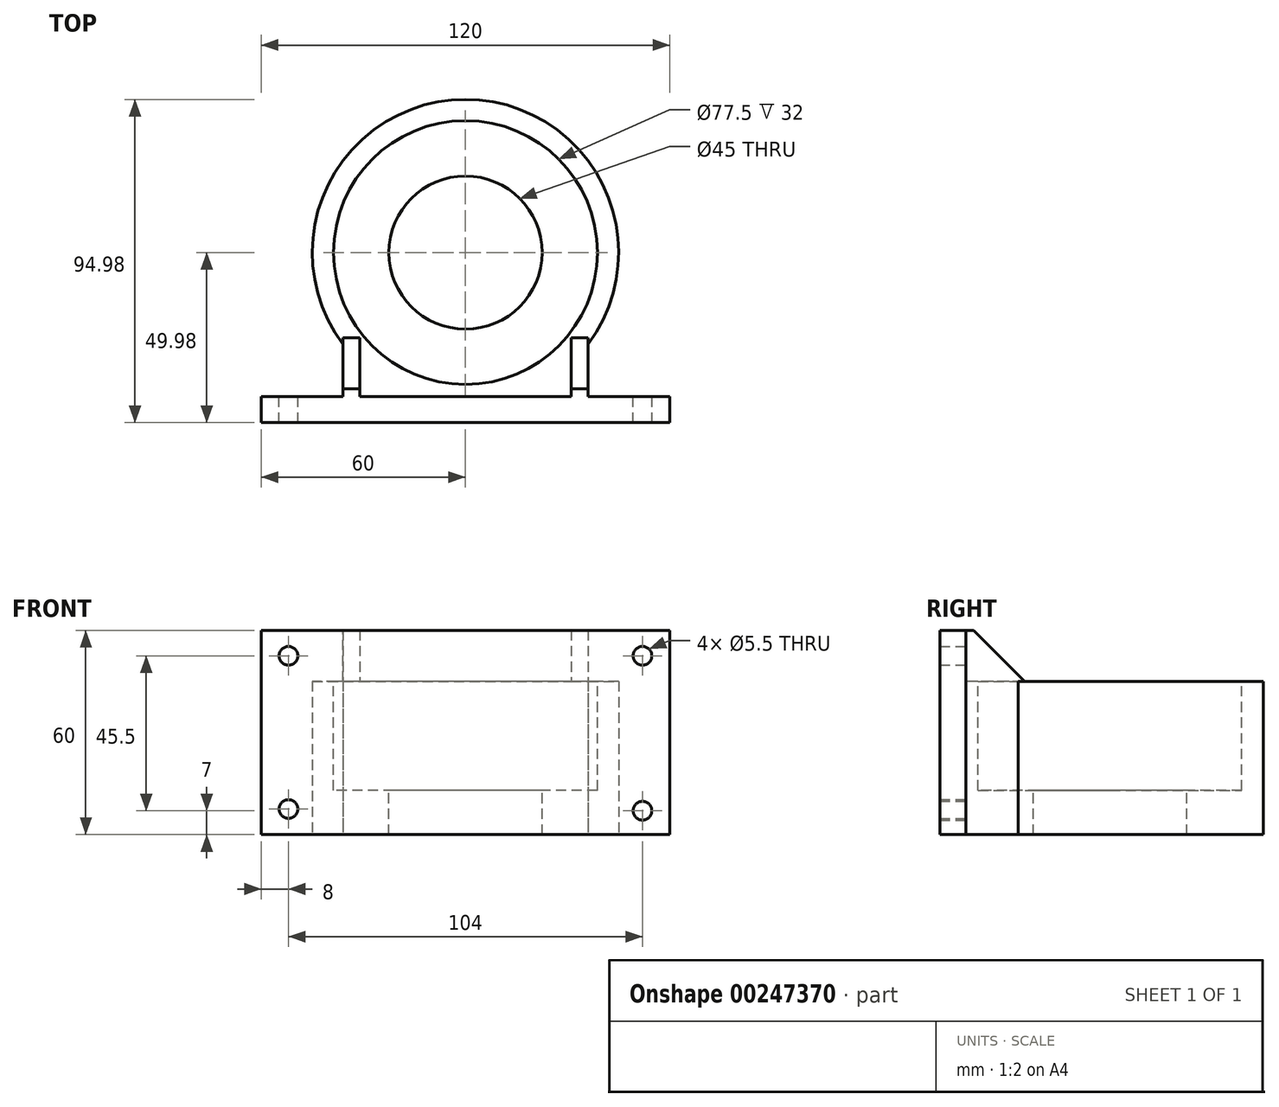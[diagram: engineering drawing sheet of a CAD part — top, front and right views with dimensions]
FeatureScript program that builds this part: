
annotation { "Feature Type Name" : "Feature", "Feature Type Description" : "" }
export const myFeature = defineFeature(function(context is Context, id is Id, definition is map)
    precondition{}
    {
        {
            var Q0;
            Q0=qCreatedBy(makeId("Top.planeOp"),FACE);
            var sketch = newSketch(context, id + "F0", { "sketchPlane" : qUnion([Q0])});
            skCircle(sketch, "E0", {"center": v(0, 0) * mm, "radius": 45 * mm});
            skLineSegment(sketch, "E1.bottom", {"start": v(-36, -27) * mm, "end": v(36, -27) * mm});
            skLineSegment(sketch, "E1.top", {"start": v(-36, -50) * mm, "end": v(36, -50) * mm});
            skLineSegment(sketch, "E1.left", {"start": v(-36, -27) * mm, "end": v(-36, -50) * mm});
            skLineSegment(sketch, "E1.right", {"start": v(36, -27) * mm, "end": v(36, -50) * mm});
            skLineSegment(sketch, "E2.bottom", {"start": v(-60, -42.37) * mm, "end": v(60, -42.37) * mm});
            skLineSegment(sketch, "E2.top", {"start": v(-60, -49.98) * mm, "end": v(60, -49.98) * mm});
            skLineSegment(sketch, "E2.left", {"start": v(-60, -42.37) * mm, "end": v(-60, -49.98) * mm});
            skLineSegment(sketch, "E2.right", {"start": v(60, -42.37) * mm, "end": v(60, -49.98) * mm});
            skSolve(sketch);
        }
        {
            var Q0;
            {var subQ0=sQuery(id+"F0.wireOp",EDGE,"E1.bottom");Q0=makeQuery(id+"F0.imprint","IMPRINT",FACE,{"disambiguationData":[TD([[makeQuery(id+"F0.imprint","IMPRINT",EDGE,{"derivedFrom":subQ0}),1.0]])]});}
            var Q1;
            {var subQ0=sQuery(id+"F0.wireOp",EDGE,"E1.left");var subQ3=sQuery(id+"F0.wireOp",EDGE,"E2.bottom");var subQ5=makeQuery(id+"F0.imprint","INTERSECT",VERTEX,{"derivedFrom":[subQ0,subQ3]});Q1=makeQuery(id+"F0.imprint","IMPRINT",FACE,{"disambiguationData":[TD([[makeQuery(id+"F0.imprint","IMPRINT",EDGE,{"disambiguationData":[TD([[subQ5,-1.0]])],"derivedFrom":subQ3}),1.0]])]});}
            var Q2;
            {var subQ0=sQuery(id+"F0.wireOp",EDGE,"E1.bottom");Q2=makeQuery(id+"F0.imprint","IMPRINT",FACE,{"disambiguationData":[TD([[makeQuery(id+"F0.imprint","IMPRINT",EDGE,{"derivedFrom":subQ0}),-1.0]])]});}
            var Q3;
            {var subQ0=sQuery(id+"F0.wireOp",EDGE,"E2.bottom");var subQ1=sQuery(id+"F0.wireOp",EDGE,"E0");var subQ2=makeQuery(id+"F0.imprint","INTERSECT",VERTEX,{"disambiguationData":[OD(0.0)],"derivedFrom":[subQ1,subQ0]});Q3=makeQuery(id+"F0.imprint","IMPRINT",FACE,{"disambiguationData":[TD([[makeQuery(id+"F0.imprint","IMPRINT",EDGE,{"disambiguationData":[TD([[subQ2,-1.0]])],"derivedFrom":subQ1}),1.0]])]});}
            var Q4;
            {var subQ5=sQuery(id+"F0.wireOp",EDGE,"E2.left");Q4=makeQuery(id+"F0.imprint","IMPRINT",FACE,{"disambiguationData":[TD([[makeQuery(id+"F0.imprint","IMPRINT",EDGE,{"derivedFrom":subQ5}),1.0]])]});}
            var Q5;
            {var subQ0=sQuery(id+"F0.wireOp",EDGE,"E2.bottom");var subQ3=sQuery(id+"F0.wireOp",EDGE,"E0");var subQ4=makeQuery(id+"F0.imprint","INTERSECT",VERTEX,{"disambiguationData":[OD(0.0)],"derivedFrom":[subQ3,subQ0]});Q5=makeQuery(id+"F0.imprint","IMPRINT",FACE,{"disambiguationData":[TD([[makeQuery(id+"F0.imprint","IMPRINT",EDGE,{"disambiguationData":[TD([[subQ4,-1.0]])],"derivedFrom":subQ3}),-1.0]])]});}
            var Q6;
            {var subQ5=sQuery(id+"F0.wireOp",EDGE,"E2.right");Q6=makeQuery(id+"F0.imprint","IMPRINT",FACE,{"disambiguationData":[TD([[makeQuery(id+"F0.imprint","IMPRINT",EDGE,{"derivedFrom":subQ5}),-1.0]])]});}
            var Q7;
            {var subQ0=sQuery(id+"F0.wireOp",EDGE,"E1.right");var subQ3=sQuery(id+"F0.wireOp",EDGE,"E2.bottom");var subQ5=makeQuery(id+"F0.imprint","INTERSECT",VERTEX,{"derivedFrom":[subQ0,subQ3]});Q7=makeQuery(id+"F0.imprint","IMPRINT",FACE,{"disambiguationData":[TD([[makeQuery(id+"F0.imprint","IMPRINT",EDGE,{"disambiguationData":[TD([[subQ5,1.0]])],"derivedFrom":subQ3}),1.0]])]});}
            extrude(context, id + "F1", {"entities" : qUnion([Q0, Q1, Q2, Q3, Q4, Q5, Q6, Q7]), "depth" : 45 * mm});
        }
        {
            var Q0;
            Q0=makeQuery(id+"F1.opExtrude","CAP_FACE",FACE,{"disambiguationData":[OSD([sQuery(id+"F0.wireOp",EDGE,"E0"),sQuery(id+"F0.wireOp",EDGE,"E1.left"),sQuery(id+"F0.wireOp",EDGE,"E1.right"),sQuery(id+"F0.wireOp",EDGE,"E2.bottom"),sQuery(id+"F0.wireOp",EDGE,"E2.top"),sQuery(id+"F0.wireOp",EDGE,"E2.left"),sQuery(id+"F0.wireOp",EDGE,"E2.right")])],"isStart":false});
            var sketch = newSketch(context, id + "F2", { "sketchPlane" : qUnion([Q0])});
            skCircle(sketch, "E3", {"center": v(0, 0) * mm, "radius": 38.75 * mm});
            skSolve(sketch);
        }
        {
            var Q0;
            Q0=makeQuery(id+"F1.opExtrude","CAP_FACE",FACE,{"disambiguationData":[OSD([sQuery(id+"F0.wireOp",EDGE,"E0"),sQuery(id+"F0.wireOp",EDGE,"E1.left"),sQuery(id+"F0.wireOp",EDGE,"E1.right"),sQuery(id+"F0.wireOp",EDGE,"E2.bottom"),sQuery(id+"F0.wireOp",EDGE,"E2.top"),sQuery(id+"F0.wireOp",EDGE,"E2.left"),sQuery(id+"F0.wireOp",EDGE,"E2.right")])],"isStart":false});
            var sketch = newSketch(context, id + "F3", { "sketchPlane" : qUnion([Q0])});
            skLineSegment(sketch, "E4.bottom", {"start": v(-60, -42.37) * mm, "end": v(60, -42.37) * mm});
            skLineSegment(sketch, "E4.top", {"start": v(-60, -49.98) * mm, "end": v(60, -49.98) * mm});
            skLineSegment(sketch, "E4.left", {"start": v(-60, -42.37) * mm, "end": v(-60, -49.98) * mm});
            skLineSegment(sketch, "E4.right", {"start": v(60, -42.37) * mm, "end": v(60, -49.98) * mm});
            skSolve(sketch);
        }
        {
            var Q0;
            Q0=qSketchRegion(id+"F2",true);
            extrude(context, id + "F4", {"entities" : qUnion([Q0]), "operationType" : NewBodyOperationType.REMOVE, "oppositeDirection" : true, "depth" : 32 * mm});
        }
        {
            var Q0;
            Q0=makeQuery(id+"F3.imprint","IMPRINT",FACE,{"disambiguationData":[TD([[makeQuery(id+"F3.imprint","IMPRINT",EDGE,{"derivedFrom":sQuery(id+"F3.wireOp",EDGE,"E4.top")}),1.0]])]});
            extrude(context, id + "F5", {"entities" : qUnion([Q0]), "operationType" : NewBodyOperationType.ADD, "depth" : 15 * mm});
        }
        {
            var Q0;
            Q0=makeQuery(id+"F1.opExtrude","CAP_FACE",FACE,{"disambiguationData":[OSD([sQuery(id+"F0.wireOp",EDGE,"E0"),sQuery(id+"F0.wireOp",EDGE,"E1.left"),sQuery(id+"F0.wireOp",EDGE,"E1.right"),sQuery(id+"F0.wireOp",EDGE,"E2.bottom"),sQuery(id+"F0.wireOp",EDGE,"E2.top"),sQuery(id+"F0.wireOp",EDGE,"E2.left"),sQuery(id+"F0.wireOp",EDGE,"E2.right")])],"isStart":false});
            var sketch = newSketch(context, id + "F6", { "sketchPlane" : qUnion([Q0])});
            skLineSegment(sketch, "E5.bottom", {"start": v(-36, -25.03) * mm, "end": v(-31, -25.03) * mm});
            skLineSegment(sketch, "E5.top", {"start": v(-36, -42.53) * mm, "end": v(-31, -42.53) * mm});
            skLineSegment(sketch, "E5.left", {"start": v(-36, -25.03) * mm, "end": v(-36, -42.53) * mm});
            skLineSegment(sketch, "E5.right", {"start": v(-31, -25.03) * mm, "end": v(-31, -42.53) * mm});
            skLineSegment(sketch, "E6.bottom", {"start": v(31, -25.03) * mm, "end": v(36, -25.03) * mm});
            skLineSegment(sketch, "E6.top", {"start": v(31, -42.53) * mm, "end": v(36, -42.53) * mm});
            skLineSegment(sketch, "E6.left", {"start": v(31, -25.03) * mm, "end": v(31, -42.53) * mm});
            skLineSegment(sketch, "E6.right", {"start": v(36, -25.03) * mm, "end": v(36, -42.53) * mm});
            skSolve(sketch);
        }
        {
            var Q0;
            {var subQ0=sQuery(id+"F6.wireOp",EDGE,"E5.bottom");Q0=makeQuery(id+"F6.imprint","IMPRINT",FACE,{"disambiguationData":[TD([[makeQuery(id+"F6.imprint","IMPRINT",EDGE,{"derivedFrom":subQ0}),-1.0]])]});}
            var Q1;
            {var subQ0=sQuery(id+"F6.wireOp",EDGE,"E6.bottom");Q1=makeQuery(id+"F6.imprint","IMPRINT",FACE,{"disambiguationData":[TD([[makeQuery(id+"F6.imprint","IMPRINT",EDGE,{"derivedFrom":subQ0}),-1.0]])]});}
            extrude(context, id + "F7", {"entities" : qUnion([Q0, Q1]), "operationType" : NewBodyOperationType.ADD, "depth" : 15 * mm});
        }
        {
            var Q0;
            Q0=makeQuery(id+"F7.opExtrude","CAP_EDGE",EDGE,{"disambiguationData":[OSD([sQuery(id+"F6.wireOp",EDGE,"E5.bottom")])],"isStart":false});
            var Q1;
            Q1=makeQuery(id+"F7.opExtrude","CAP_EDGE",EDGE,{"disambiguationData":[OSD([sQuery(id+"F6.wireOp",EDGE,"E6.bottom")])],"isStart":false});
            chamfer(context, id + "F8", {"entities" : qUnion([Q0, Q1]), "width" : 15 * mm, "tangentPropagation" : true});
        }
        {
            var Q0;
            {var subQ0=sQuery(id+"F0.wireOp",EDGE,"E2.left");var subQ1=sQuery(id+"F0.wireOp",EDGE,"E2.right");var subQ3=sQuery(id+"F0.wireOp",EDGE,"E2.bottom");var subQ5=sQuery(id+"F0.wireOp",EDGE,"E1.left");var subQ9=sQuery(id+"F3.wireOp",EDGE,"E4.bottom");Q0=makeQuery(id+"F7.boolean.opBoolean","SPLIT",FACE,{"disambiguationData":[TD([makeQuery(id+"F1.opExtrude","SWEPT_FACE",FACE,{"disambiguationData":[OSD([subQ5])]})])],"derivedFrom":makeQuery(id+"F5.boolean.opBoolean","MERGE",FACE,{"derivedFrom":[makeQuery(id+"F1.opExtrude","SWEPT_FACE",FACE,{"disambiguationData":[OSD([subQ3]),TDD([makeQuery(id+"F0.imprint","IMPRINT",EDGE,{"disambiguationData":[TD([[makeQuery(id+"F0.imprint","INTERSECT",VERTEX,{"derivedFrom":[subQ3,subQ0]}),-1.0]])],"derivedFrom":subQ3})])]}),makeQuery(id+"F1.opExtrude","SWEPT_FACE",FACE,{"disambiguationData":[OSD([subQ3]),TDD([makeQuery(id+"F0.imprint","IMPRINT",EDGE,{"disambiguationData":[TD([[makeQuery(id+"F0.imprint","INTERSECT",VERTEX,{"derivedFrom":[subQ3,subQ1]}),1.0]])],"derivedFrom":subQ3})])]}),makeQuery(id+"F5.opExtrude","SWEPT_FACE",FACE,{"disambiguationData":[OSD([subQ9])]})]})});}
            var sketch = newSketch(context, id + "F9", { "sketchPlane" : qUnion([Q0])});
            skCircle(sketch, "E7", {"center": v(52, 7.5) * mm, "radius": 2.75 * mm});
            skCircle(sketch, "E8", {"center": v(52, 52.5) * mm, "radius": 2.75 * mm});
            skCircle(sketch, "E9", {"center": v(-52, 7) * mm, "radius": 2.75 * mm});
            skCircle(sketch, "E10", {"center": v(-52, 52.5) * mm, "radius": 2.75 * mm});
            skSolve(sketch);
        }
        {
            var Q0;
            Q0=makeQuery(id+"F9.imprint","IMPRINT",FACE,{"disambiguationData":[TD([[makeQuery(id+"F9.imprint","IMPRINT",EDGE,{"derivedFrom":sQuery(id+"F9.wireOp",EDGE,"E7")}),1.0]])]});
            var Q1;
            Q1=makeQuery(id+"F9.imprint","IMPRINT",FACE,{"disambiguationData":[TD([[makeQuery(id+"F9.imprint","IMPRINT",EDGE,{"derivedFrom":sQuery(id+"F9.wireOp",EDGE,"E8")}),1.0]])]});
            var Q2;
            Q2=makeQuery(id+"F9.imprint","IMPRINT",FACE,{"disambiguationData":[TD([[makeQuery(id+"F9.imprint","IMPRINT",EDGE,{"derivedFrom":sQuery(id+"F9.wireOp",EDGE,"E9")}),1.0]])]});
            var Q3;
            Q3=makeQuery(id+"F9.imprint","IMPRINT",FACE,{"disambiguationData":[TD([[makeQuery(id+"F9.imprint","IMPRINT",EDGE,{"derivedFrom":sQuery(id+"F9.wireOp",EDGE,"E10")}),1.0]])]});
            extrude(context, id + "F10", {"entities" : qUnion([Q0, Q1, Q2, Q3]), "operationType" : NewBodyOperationType.REMOVE, "oppositeDirection" : true, "depth" : 25 * mm});
        }
        {
            var Q0;
            Q0=makeQuery(id+"F4.boolean.opBoolean","COPY",FACE,{"derivedFrom":makeQuery(id+"F4.opExtrude","CAP_FACE",FACE,{"disambiguationData":[OSD([sQuery(id+"F2.wireOp",EDGE,"E3")])],"isStart":false})});
            var sketch = newSketch(context, id + "F11", { "sketchPlane" : qUnion([Q0])});
            skCircle(sketch, "E11", {"center": v(0, 0) * mm, "radius": 22.5 * mm});
            skSolve(sketch);
        }
        {
            var Q0;
            Q0=makeQuery(id+"F11.imprint","IMPRINT",FACE,{"disambiguationData":[TD([[makeQuery(id+"F11.imprint","IMPRINT",EDGE,{"derivedFrom":sQuery(id+"F11.wireOp",EDGE,"E11")}),1.0]])]});
            extrude(context, id + "F12", {"entities" : qUnion([Q0]), "operationType" : NewBodyOperationType.REMOVE, "oppositeDirection" : true, "depth" : 25 * mm});
        }
    });
